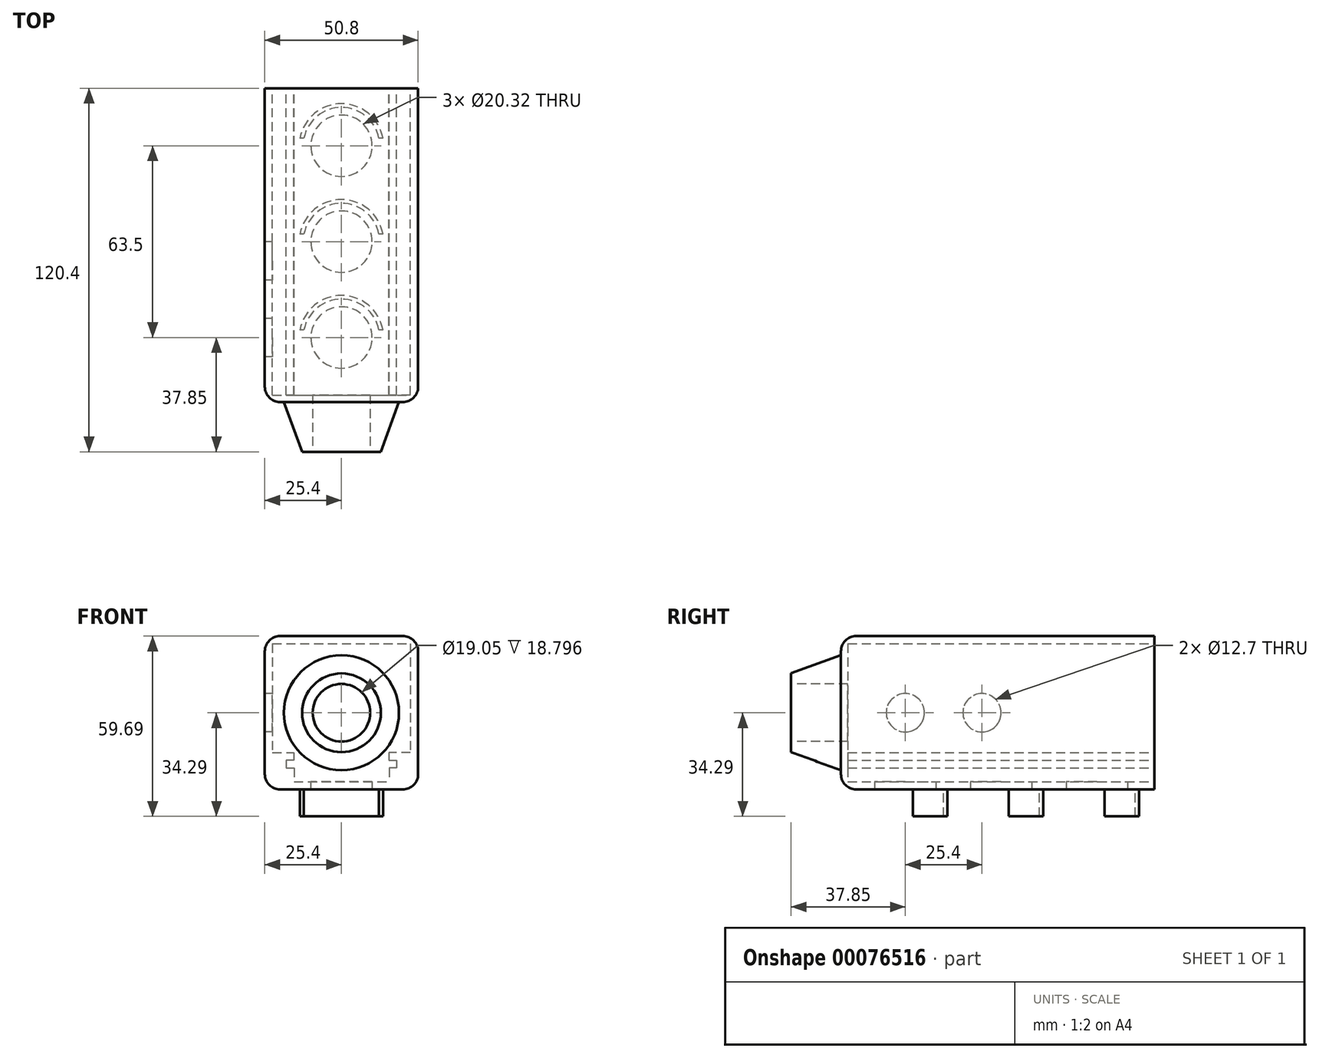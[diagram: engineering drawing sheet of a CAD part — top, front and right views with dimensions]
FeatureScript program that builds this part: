
annotation { "Feature Type Name" : "Feature", "Feature Type Description" : "" }
export const myFeature = defineFeature(function(context is Context, id is Id, definition is map)
    precondition{}
    {
        {
            var Q0;
            Q0=qCreatedBy(makeId("Front.planeOp"),FACE);
            var sketch = newSketch(context, id + "F0", { "sketchPlane" : qUnion([Q0])});
            skLineSegment(sketch, "E0.bottom", {"start": v(-50.8, 50.8) * mm, "end": v(0, 50.8) * mm});
            skLineSegment(sketch, "E0.top", {"start": v(-50.8, 0) * mm, "end": v(0, 0) * mm});
            skLineSegment(sketch, "E0.left", {"start": v(-50.8, 50.8) * mm, "end": v(-50.8, 0) * mm});
            skLineSegment(sketch, "E0.right", {"start": v(0, 50.8) * mm, "end": v(0, 0) * mm});
            skLineSegment(sketch, "E1.0", {"start": v(-48.26, 48.26) * mm, "end": v(-2.54, 48.26) * mm});
            skLineSegment(sketch, "E1.1", {"start": v(-48.26, 48.26) * mm, "end": v(-48.26, 12.2) * mm});
            skLineSegment(sketch, "E1.2", {"start": v(-41.1, 2.54) * mm, "end": v(-9.6, 2.54) * mm});
            skLineSegment(sketch, "E1.3", {"start": v(-2.54, 48.26) * mm, "end": v(-2.54, 12.2) * mm});
            skLineSegment(sketch, "E2", {"start": v(-48.26, 12.2) * mm, "end": v(-41.15, 12.2) * mm});
            skLineSegment(sketch, "E3", {"start": v(-41.15, 12.2) * mm, "end": v(-41.15, 9.65) * mm});
            skLineSegment(sketch, "E4", {"start": v(-41.15, 9.65) * mm, "end": v(-43.69, 9.65) * mm});
            skLineSegment(sketch, "E5", {"start": v(-43.69, 9.65) * mm, "end": v(-43.69, 7.11) * mm});
            skLineSegment(sketch, "E6", {"start": v(-43.69, 7.11) * mm, "end": v(-41.1, 7.11) * mm});
            skLineSegment(sketch, "E7", {"start": v(-41.1, 7.11) * mm, "end": v(-41.1, 2.54) * mm});
            skLineSegment(sketch, "E8", {"start": v(-2.54, 12.2) * mm, "end": v(-9.65, 12.2) * mm});
            skLineSegment(sketch, "E9", {"start": v(-9.65, 12.2) * mm, "end": v(-9.65, 9.65) * mm});
            skLineSegment(sketch, "E10", {"start": v(-9.65, 9.65) * mm, "end": v(-7.11, 9.65) * mm});
            skLineSegment(sketch, "E11", {"start": v(-7.11, 9.65) * mm, "end": v(-7.11, 7.11) * mm});
            skLineSegment(sketch, "E12", {"start": v(-7.11, 7.11) * mm, "end": v(-9.6, 7.11) * mm});
            skLineSegment(sketch, "E13", {"start": v(-9.6, 7.11) * mm, "end": v(-9.6, 2.54) * mm});
            skSolve(sketch);
        }
        {
            var Q0;
            Q0 = qSketchRegion(id + "F0", true);
            extrude(context, id + "F1", {"entities" : qUnion([Q0]), "depth" : 101.6 * mm});
        }
        {
            var Q0;
            Q0=makeQuery(id+"F1.opExtrude","SWEPT_FACE",FACE,{"disambiguationData":[OSD([sQuery(id+"F0.wireOp",EDGE,"E0.left")])]});
            var sketch = newSketch(context, id + "F2", { "sketchPlane" : qUnion([Q0])});
            skLineSegment(sketch, "E14", {"start": v(0, 25.4) * mm, "end": v(101.6, 25.4) * mm});
            skCircle(sketch, "E15", {"center": v(82.55, 25.4) * mm, "radius": 6.35 * mm});
            skCircle(sketch, "E16", {"center": v(57.15, 25.4) * mm, "radius": 6.35 * mm});
            skSolve(sketch);
        }
        {
            var Q0;
            Q0 = qSketchRegion(id + "F2", true);
            extrude(context, id + "F3", {"entities" : qUnion([Q0]), "operationType" : NewBodyOperationType.REMOVE, "oppositeDirection" : true, "depth" : 12.7 * mm});
        }
        {
            var Q0;
            Q0=makeQuery(id+"F1.opExtrude","SWEPT_FACE",FACE,{"disambiguationData":[OSD([sQuery(id+"F0.wireOp",EDGE,"E0.top")])]});
            var sketch = newSketch(context, id + "F4", { "sketchPlane" : qUnion([Q0])});
            skLineSegment(sketch, "E17", {"start": v(-25.4, 0) * mm, "end": v(-25.4, 101.6) * mm});
            skCircle(sketch, "E18", {"center": v(-25.4, 19.05) * mm, "radius": 10.16 * mm});
            skCircle(sketch, "E19", {"center": v(-25.4, 50.8) * mm, "radius": 10.16 * mm});
            skCircle(sketch, "E20", {"center": v(-25.4, 82.55) * mm, "radius": 10.16 * mm});
            skSolve(sketch);
        }
        {
            var Q0;
            Q0 = qSketchRegion(id + "F4", true);
            extrude(context, id + "F5", {"entities" : qUnion([Q0]), "operationType" : NewBodyOperationType.REMOVE, "oppositeDirection" : true, "depth" : 25.4 * mm});
        }
        {
            var Q0;
            Q0=makeQuery(id+"F1.opExtrude","SWEPT_FACE",FACE,{"disambiguationData":[OSD([sQuery(id+"F0.wireOp",EDGE,"E0.top")])]});
            var sketch = newSketch(context, id + "F6", { "sketchPlane" : qUnion([Q0])});
            skArc(sketch, "E21", {"start": v(-37.84, 16.5) * mm, "mid": v(-25.4, 6.35) * mm, "end": v(-12.96, 16.51) * mm});
            skArc(sketch, "E22", {"start": v(-39.14, 16.5) * mm, "mid": v(-25.4, 5.08) * mm, "end": v(-11.66, 16.51) * mm});
            skLineSegment(sketch, "E23", {"start": v(-11.66, 16.51) * mm, "end": v(-12.96, 16.51) * mm});
            skLineSegment(sketch, "E24.trimOffspring", {"start": v(-37.84, 16.5) * mm, "end": v(-39.14, 16.5) * mm});
            skArc(sketch, "E25", {"start": v(-37.84, 48.26) * mm, "mid": v(-25.4, 38.1) * mm, "end": v(-12.96, 48.26) * mm});
            skArc(sketch, "E26", {"start": v(-39.14, 48.26) * mm, "mid": v(-25.4, 36.83) * mm, "end": v(-11.66, 48.26) * mm});
            skLineSegment(sketch, "E27", {"start": v(-11.66, 48.26) * mm, "end": v(-12.96, 48.26) * mm});
            skLineSegment(sketch, "E28.trimOffspring", {"start": v(-37.84, 48.26) * mm, "end": v(-39.14, 48.26) * mm});
            skArc(sketch, "E29", {"start": v(-37.84, 80.01) * mm, "mid": v(-25.4, 69.85) * mm, "end": v(-12.96, 80.01) * mm});
            skArc(sketch, "E30", {"start": v(-39.14, 80.01) * mm, "mid": v(-25.4, 68.58) * mm, "end": v(-11.66, 80.01) * mm});
            skLineSegment(sketch, "E31", {"start": v(-11.66, 80.01) * mm, "end": v(-12.96, 80.01) * mm});
            skLineSegment(sketch, "E32.trimOffspring", {"start": v(-37.84, 80.01) * mm, "end": v(-39.14, 80.01) * mm});
            skSolve(sketch);
        }
        {
            var Q0;
            Q0 = qSketchRegion(id + "F6", true);
            extrude(context, id + "F7", {"entities" : qUnion([Q0]), "operationType" : NewBodyOperationType.ADD, "depth" : 8.9 * mm});
        }
        {
            var Q0;
            Q0=makeQuery(id+"F1.opExtrude","CAP_FACE",FACE,{"disambiguationData":[OSD([sQuery(id+"F0.wireOp",EDGE,"E0.bottom"),sQuery(id+"F0.wireOp",EDGE,"E0.top"),sQuery(id+"F0.wireOp",EDGE,"E0.left"),sQuery(id+"F0.wireOp",EDGE,"E0.right"),sQuery(id+"F0.wireOp",EDGE,"E1.0"),sQuery(id+"F0.wireOp",EDGE,"E1.1"),sQuery(id+"F0.wireOp",EDGE,"E1.2"),sQuery(id+"F0.wireOp",EDGE,"E1.3"),sQuery(id+"F0.wireOp",EDGE,"E2"),sQuery(id+"F0.wireOp",EDGE,"E3"),sQuery(id+"F0.wireOp",EDGE,"E4"),sQuery(id+"F0.wireOp",EDGE,"E5"),sQuery(id+"F0.wireOp",EDGE,"E6"),sQuery(id+"F0.wireOp",EDGE,"E7"),sQuery(id+"F0.wireOp",EDGE,"E8"),sQuery(id+"F0.wireOp",EDGE,"E9"),sQuery(id+"F0.wireOp",EDGE,"E10"),sQuery(id+"F0.wireOp",EDGE,"E11"),sQuery(id+"F0.wireOp",EDGE,"E12"),sQuery(id+"F0.wireOp",EDGE,"E13")])],"isStart":false});
            var sketch = newSketch(context, id + "F8", { "sketchPlane" : qUnion([Q0])});
            skLineSegment(sketch, "E33.bottom", {"start": v(-50.8, 0) * mm, "end": v(0, 0) * mm});
            skLineSegment(sketch, "E33.top", {"start": v(-50.8, 50.8) * mm, "end": v(0, 50.8) * mm});
            skLineSegment(sketch, "E33.left", {"start": v(-50.8, 0) * mm, "end": v(-50.8, 50.8) * mm});
            skLineSegment(sketch, "E33.right", {"start": v(0, 0) * mm, "end": v(0, 50.8) * mm});
            skSolve(sketch);
        }
        {
            var Q0;
            Q0 = qSketchRegion(id + "F8", true);
            extrude(context, id + "F9", {"entities" : qUnion([Q0]), "operationType" : NewBodyOperationType.ADD, "depth" : 2.3 * mm});
        }
        {
            var Q0;
            Q0=makeQuery(id+"F9.opExtrude","CAP_FACE",FACE,{"disambiguationData":[OSD([sQuery(id+"F8.wireOp",EDGE,"E33.bottom"),sQuery(id+"F8.wireOp",EDGE,"E33.top"),sQuery(id+"F8.wireOp",EDGE,"E33.left"),sQuery(id+"F8.wireOp",EDGE,"E33.right")])],"isStart":false});
            var sketch = newSketch(context, id + "F10", { "sketchPlane" : qUnion([Q0])});
            skLineSegment(sketch, "E34", {"start": v(-25.4, 50.8) * mm, "end": v(-25.4, 0) * mm, "construction": true});
            skLineSegment(sketch, "E35", {"start": v(0, 25.4) * mm, "end": v(-50.8, 25.4) * mm, "construction": true});
            skCircle(sketch, "E36", {"center": v(-25.4, 25.4) * mm, "radius": 19.05 * mm});
            skSolve(sketch);
        }
        {
            var Q0;
            Q0 = qSketchRegion(id + "F10", true);
            extrude(context, id + "F11", {"entities" : qUnion([Q0]), "operationType" : NewBodyOperationType.ADD, "depth" : 16.5 * mm, "hasDraft" : true, "draftAngle" : 20 * degree, "draftPullDirection" : true});
        }
        {
            var Q0;
            Q0=makeQuery(id+"F11.opExtrude","CAP_FACE",FACE,{"disambiguationData":[OSD([sQuery(id+"F10.wireOp",EDGE,"E36")])],"isStart":false});
            var sketch = newSketch(context, id + "F12", { "sketchPlane" : qUnion([Q0])});
            skCircle(sketch, "E37", {"center": v(-25.4, 25.4) * mm, "radius": 9.53 * mm});
            skSolve(sketch);
        }
        {
            var Q0;
            Q0 = qSketchRegion(id + "F12", true);
            extrude(context, id + "F13", {"entities" : qUnion([Q0]), "operationType" : NewBodyOperationType.REMOVE, "oppositeDirection" : true, "depth" : 25.4 * mm});
        }
        {
            var Q0;
            Q0=makeQuery(id+"F9.boolean.opBoolean","MERGE",EDGE,{"derivedFrom":[makeQuery(id+"F1.opExtrude","SWEPT_EDGE",EDGE,{"disambiguationData":[OSD([sQuery(id+"F0.wireOp",EDGE,"E0.top"),sQuery(id+"F0.wireOp",EDGE,"E0.right")])]}),makeQuery(id+"F9.opExtrude","SWEPT_EDGE",EDGE,{"disambiguationData":[OSD([sQuery(id+"F8.wireOp",EDGE,"E33.bottom"),sQuery(id+"F8.wireOp",EDGE,"E33.right")])]})]});
            var Q1;
            Q1=makeQuery(id+"F9.boolean.opBoolean","MERGE",EDGE,{"derivedFrom":[makeQuery(id+"F1.opExtrude","SWEPT_EDGE",EDGE,{"disambiguationData":[OSD([sQuery(id+"F0.wireOp",EDGE,"E0.top"),sQuery(id+"F0.wireOp",EDGE,"E0.left")])]}),makeQuery(id+"F9.opExtrude","SWEPT_EDGE",EDGE,{"disambiguationData":[OSD([sQuery(id+"F8.wireOp",EDGE,"E33.bottom"),sQuery(id+"F8.wireOp",EDGE,"E33.left")])]})]});
            var Q2;
            Q2=makeQuery(id+"F9.boolean.opBoolean","MERGE",EDGE,{"derivedFrom":[makeQuery(id+"F1.opExtrude","SWEPT_EDGE",EDGE,{"disambiguationData":[OSD([sQuery(id+"F0.wireOp",EDGE,"E0.bottom"),sQuery(id+"F0.wireOp",EDGE,"E0.left")])]}),makeQuery(id+"F9.opExtrude","SWEPT_EDGE",EDGE,{"disambiguationData":[OSD([sQuery(id+"F8.wireOp",EDGE,"E33.top"),sQuery(id+"F8.wireOp",EDGE,"E33.left")])]})]});
            var Q3;
            Q3=makeQuery(id+"F9.boolean.opBoolean","MERGE",EDGE,{"derivedFrom":[makeQuery(id+"F1.opExtrude","SWEPT_EDGE",EDGE,{"disambiguationData":[OSD([sQuery(id+"F0.wireOp",EDGE,"E0.bottom"),sQuery(id+"F0.wireOp",EDGE,"E0.right")])]}),makeQuery(id+"F9.opExtrude","SWEPT_EDGE",EDGE,{"disambiguationData":[OSD([sQuery(id+"F8.wireOp",EDGE,"E33.top"),sQuery(id+"F8.wireOp",EDGE,"E33.right")])]})]});
            fillet(context, id + "F14", {"entities" : qUnion([Q0, Q1, Q2, Q3]), "radius" : 5.08 * mm, "tangentPropagation" : true, "allowEdgeOverflow" : false});
        }
        {
            var Q0;
            Q0=makeQuery(id+"F9.opExtrude","CAP_EDGE",EDGE,{"disambiguationData":[OSD([sQuery(id+"F8.wireOp",EDGE,"E33.top")])],"isStart":false});
            fillet(context, id + "F15", {"entities" : qUnion([Q0]), "radius" : 5.08 * mm, "tangentPropagation" : true, "allowEdgeOverflow" : false});
        }
    });
